# Revit family: halyxx_671736_004_1_89_e546
name_source: partatom
category: Lighting Fixtures
units: mm (PartAtom-declared; Revit-internal decimal feet)

## family parameters
Cut with Voids When Loaded = No
Host = Face
Light Source = No
Part Type = Normal
Room Calculation Point = No
Round Connector Dimension = Use Diameter
Shared = No

## types (1)
- HALYXX (1 x LED Modul 840, 60 lm, 4000)
    Apparent Load = 3 VA
    Approval mark = CE
    CIE Flux Codes = 18 46 76 54 100
    Color Rendering = 80
    Color Temperature = 4000
    Default Elevation = 1800 mm
    Description = Series: HALYXX
Luminaire for escape route identification. Housing: extruded aluminium profile, anodised or powder-coated. Display panel: highly transparent panel, plastic, with legend on one side/both sides. Driver integrated. Suitable for connection to central battery systems. With AC Control monitoring module for LUXIFAIR central battery units. Please indicate legend number when placing your order! 
Colour: anodised aluminium
Length: 235 mm
Width: 40 mm
Height: 220 mm
Weight: 1.35 kg
Operating mode: maintained power mode
Viewing Distance: 19 m
Lamp: LED
Socket: without socket
Colour temperature: 4000K
Colour rendering index (CRI): 80
System power: 3 W
Rated luminous flux: 60 lm
Luminous flux, emergency: 60
System power, emergency: 2.8 W
Control gear: Regulated power supply
Protection class: I
Type of protection: IP 40
    Height = 220 mm
    Lamp = 1 x LED Modul 840
    Lamp Light Flux = 60 lm
    Lamp count = 1
    Length = 235 mm
    Lifetime = 50000 h
    Luminous efficacy = 20 lm/W
    Manufacturer = RZB
    ModVariant = No
    Model = 671736.004.1.89
    Mounting Place = Ceiling
    Mounting Type = Surface mounted
    Number of Poles = 1
    OnlyDefault = Yes
    Power Factor = 1
    Product Name = HALYXX
    Product group = Surface mounted ceiling luminaires
    ProductGroupID = 303
    Protection Class = Protection class I
    Protection Degree = IP 40
    RLX_Detail_Level = 1
    RLX_Emergency_Light_Flux = 60 lm
    RLX_Emergency_Type = 3
    RLX_Emergency_Type_DB = Yes
    RlxData = <blob elided: 42909 chars, md5=bfcf71ac>
    Socket = socket
    Standby Power = 0 W
    System Light Flux = 60 lm
    System Power = 3 W
    Type Comments = Product without accessories
    Type Image = 671742.004.jpg
    URL = http://relux.com
    VarID = ---
    Voltage = 230 V
    Voltage Range = 220-240 V
    Weight = 0.00 kg
    Width = 40 mm  [stored 0.131234 ft]

note: [stored X ft] marks values corroborated as IEEE doubles in the binary element streams (Revit-internal decimal feet)

## geometry (parser evidence)
native form markers: Sweep x11
no freeform markers — native parametric forms only
